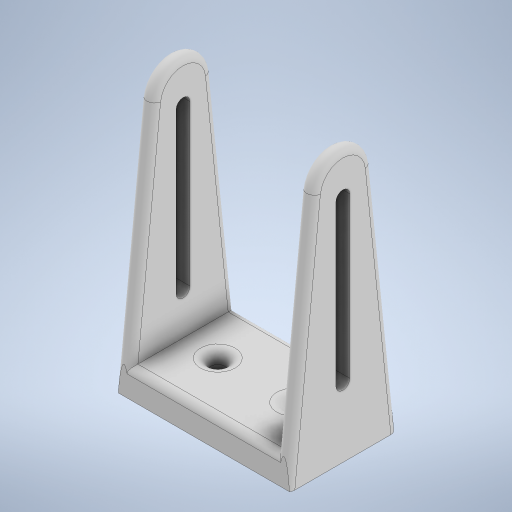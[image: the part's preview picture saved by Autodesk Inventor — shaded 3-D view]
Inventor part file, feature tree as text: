
AUTODESK INVENTOR PART (.ipt)
format: ipt  version: 2023 (Build 270158000, 158)  size: 552,960 bytes
history: native  units: mm
features: extrude x4, chamfer x4, fillet x4, sketch x4, other x1
ambient origin geometry x8: Origin, YZ Plane, XZ Plane, XY Plane, X Axis, Y Axis, Z Axis, Center Point
bodies: Body1 (feature_tree)
feature tree (17):
  other  "Bryła1"
  extrude  "Wyciągnięcie proste1"  Depth=50.0mm
  extrude  "Wyciągnięcie proste2"  Depth=30.0mm
  chamfer  "Faza1"  Distance=8.0mm
  chamfer  "Faza2"  Distance=4.0mm
  chamfer  "Faza3"  Distance=4.0mm
  chamfer  "Faza4"  Distance=70.0mm
  extrude  "Wyciągnięcie proste3"  Depth=2.0mm
  extrude  "Wyciągnięcie proste4"  Depth=2.0mm
  fillet  "Zaokrąglenie1"  Radius=2.0mm
  fillet  "Zaokrąglenie2"  Radius=2.0mm
  fillet  "Zaokrąglenie3"  Radius=4.0mm
  fillet  "Zaokrąglenie4"  Radius=10.040411mm
  sketch  "Szkic1"
  sketch  "Szkic2"
  sketch  "Szkic3"
  sketch  "Szkic4"
